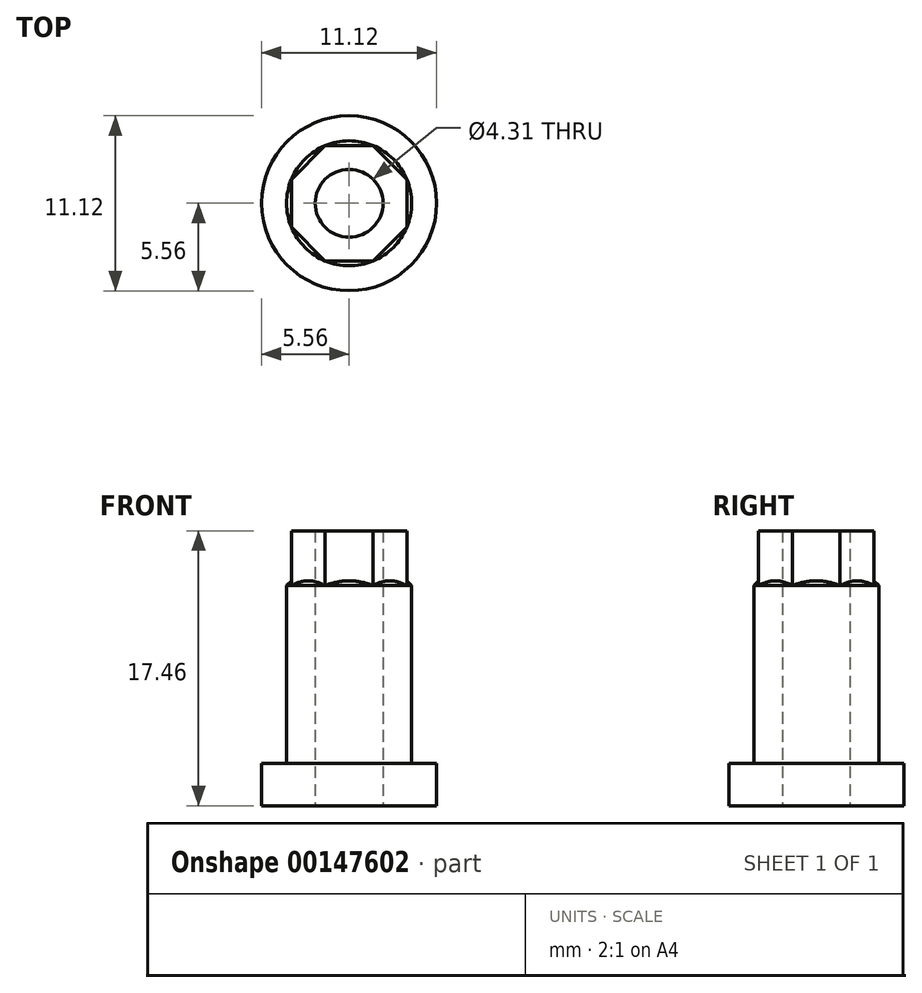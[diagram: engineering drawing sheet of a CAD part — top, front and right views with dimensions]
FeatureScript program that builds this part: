
annotation { "Feature Type Name" : "Feature", "Feature Type Description" : "" }
export const myFeature = defineFeature(function(context is Context, id is Id, definition is map)
    precondition{}
    {
        {
            var Q0;
            Q0=qCreatedBy(makeId("Top.planeOp"),FACE);
            var sketch = newSketch(context, id + "F0", { "sketchPlane" : qUnion([Q0])});
            skCircle(sketch, "E0", {"center": v(0, 0) * mm, "radius": 2.15 * mm});
            skCircle(sketch, "E1", {"center": v(0, 0) * mm, "radius": 5.56 * mm});
            skSolve(sketch);
        }
        {
            var Q0;
            Q0=qSketchRegion(id+"F0",true);
            extrude(context, id + "F1", {"entities" : qUnion([Q0]), "depth" : 2.7 * mm});
        }
        {
            var Q0;
            Q0=makeQuery(id+"F1.opExtrude","CAP_FACE",FACE,{"disambiguationData":[OSD([sQuery(id+"F0.wireOp",EDGE,"E0"),sQuery(id+"F0.wireOp",EDGE,"E1")])],"isStart":false});
            var sketch = newSketch(context, id + "F2", { "sketchPlane" : qUnion([Q0])});
            skCircle(sketch, "E2", {"center": v(0, 0) * mm, "radius": 2.15 * mm});
            skCircle(sketch, "E3", {"center": v(0, 0) * mm, "radius": 3.97 * mm});
            skSolve(sketch);
        }
        {
            var Q0;
            Q0=qSketchRegion(id+"F2",true);
            extrude(context, id + "F3", {"entities" : qUnion([Q0]), "operationType" : NewBodyOperationType.ADD, "depth" : 11.6 * mm});
        }
        {
            var Q0;
            Q0=makeQuery(id+"F3.opExtrude","CAP_FACE",FACE,{"disambiguationData":[OSD([sQuery(id+"F2.wireOp",EDGE,"E2"),sQuery(id+"F2.wireOp",EDGE,"E3")])],"isStart":false});
            var sketch = newSketch(context, id + "F4", { "sketchPlane" : qUnion([Q0])});
            skCircle(sketch, "E4", {"center": v(0, 0) * mm, "radius": 2.15 * mm});
            skCircle(sketch, "E5.cCircle", {"center": v(0, 0) * mm, "radius": 3.67 * mm, "construction": true});
            skLineSegment(sketch, "E5.0", {"start": v(-3.67, -1.52) * mm, "end": v(-3.67, 1.52) * mm});
            skLineSegment(sketch, "E5.1", {"start": v(-3.67, 1.52) * mm, "end": v(-1.52, 3.67) * mm});
            skLineSegment(sketch, "E5.2", {"start": v(-1.52, 3.67) * mm, "end": v(1.52, 3.67) * mm});
            skLineSegment(sketch, "E5.3", {"start": v(1.52, 3.67) * mm, "end": v(3.67, 1.52) * mm});
            skLineSegment(sketch, "E5.4", {"start": v(3.67, 1.52) * mm, "end": v(3.67, -1.52) * mm});
            skLineSegment(sketch, "E5.5", {"start": v(3.67, -1.52) * mm, "end": v(1.52, -3.67) * mm});
            skLineSegment(sketch, "E5.6", {"start": v(1.52, -3.67) * mm, "end": v(-1.52, -3.67) * mm});
            skLineSegment(sketch, "E5.7", {"start": v(-1.52, -3.67) * mm, "end": v(-3.67, -1.52) * mm});
            skSolve(sketch);
        }
        {
            var Q0;
            Q0=qSketchRegion(id+"F4",true);
            extrude(context, id + "F5", {"entities" : qUnion([Q0]), "operationType" : NewBodyOperationType.ADD, "depth" : 3.17 * mm});
        }
        {
            var Q0;
            {var subQ0=sQuery(id+"F2.wireOp",EDGE,"E3");Q0=makeQuery(id+"F5.boolean.opBoolean","SPLIT",EDGE,{"disambiguationData":[TD([makeQuery(id+"F3.opExtrude","CAP_FACE",FACE,{"disambiguationData":[OSD([sQuery(id+"F2.wireOp",EDGE,"E2"),subQ0])],"isStart":false}),makeQuery(id+"F3.opExtrude","SWEPT_FACE",FACE,{"disambiguationData":[OSD([subQ0])]}),makeQuery(id+"F5.opExtrude","SWEPT_FACE",FACE,{"disambiguationData":[OSD([sQuery(id+"F4.wireOp",EDGE,"E5.0")])]}),makeQuery(id+"F5.opExtrude","SWEPT_FACE",FACE,{"disambiguationData":[OSD([sQuery(id+"F4.wireOp",EDGE,"E5.1")])]}),makeQuery(id+"F5.opExtrude","SWEPT_FACE",FACE,{"disambiguationData":[OSD([sQuery(id+"F4.wireOp",EDGE,"E5.7")])]})])],"derivedFrom":makeQuery(id+"F3.opExtrude","CAP_EDGE",EDGE,{"disambiguationData":[OSD([subQ0])],"isStart":false})});}
            var Q1;
            {var subQ0=sQuery(id+"F2.wireOp",EDGE,"E3");Q1=makeQuery(id+"F5.boolean.opBoolean","SPLIT",EDGE,{"disambiguationData":[TD([makeQuery(id+"F3.opExtrude","CAP_FACE",FACE,{"disambiguationData":[OSD([sQuery(id+"F2.wireOp",EDGE,"E2"),subQ0])],"isStart":false}),makeQuery(id+"F3.opExtrude","SWEPT_FACE",FACE,{"disambiguationData":[OSD([subQ0])]}),makeQuery(id+"F5.opExtrude","SWEPT_FACE",FACE,{"disambiguationData":[OSD([sQuery(id+"F4.wireOp",EDGE,"E5.0")])]}),makeQuery(id+"F5.opExtrude","SWEPT_FACE",FACE,{"disambiguationData":[OSD([sQuery(id+"F4.wireOp",EDGE,"E5.1")])]}),makeQuery(id+"F5.opExtrude","SWEPT_FACE",FACE,{"disambiguationData":[OSD([sQuery(id+"F4.wireOp",EDGE,"E5.2")])]})])],"derivedFrom":makeQuery(id+"F3.opExtrude","CAP_EDGE",EDGE,{"disambiguationData":[OSD([subQ0])],"isStart":false})});}
            var Q2;
            {var subQ0=sQuery(id+"F2.wireOp",EDGE,"E3");Q2=makeQuery(id+"F5.boolean.opBoolean","SPLIT",EDGE,{"disambiguationData":[TD([makeQuery(id+"F3.opExtrude","CAP_FACE",FACE,{"disambiguationData":[OSD([sQuery(id+"F2.wireOp",EDGE,"E2"),subQ0])],"isStart":false}),makeQuery(id+"F3.opExtrude","SWEPT_FACE",FACE,{"disambiguationData":[OSD([subQ0])]}),makeQuery(id+"F5.opExtrude","SWEPT_FACE",FACE,{"disambiguationData":[OSD([sQuery(id+"F4.wireOp",EDGE,"E5.1")])]}),makeQuery(id+"F5.opExtrude","SWEPT_FACE",FACE,{"disambiguationData":[OSD([sQuery(id+"F4.wireOp",EDGE,"E5.2")])]}),makeQuery(id+"F5.opExtrude","SWEPT_FACE",FACE,{"disambiguationData":[OSD([sQuery(id+"F4.wireOp",EDGE,"E5.3")])]})])],"derivedFrom":makeQuery(id+"F3.opExtrude","CAP_EDGE",EDGE,{"disambiguationData":[OSD([subQ0])],"isStart":false})});}
            var Q3;
            {var subQ0=sQuery(id+"F2.wireOp",EDGE,"E3");Q3=makeQuery(id+"F5.boolean.opBoolean","SPLIT",EDGE,{"disambiguationData":[TD([makeQuery(id+"F3.opExtrude","CAP_FACE",FACE,{"disambiguationData":[OSD([sQuery(id+"F2.wireOp",EDGE,"E2"),subQ0])],"isStart":false}),makeQuery(id+"F3.opExtrude","SWEPT_FACE",FACE,{"disambiguationData":[OSD([subQ0])]}),makeQuery(id+"F5.opExtrude","SWEPT_FACE",FACE,{"disambiguationData":[OSD([sQuery(id+"F4.wireOp",EDGE,"E5.2")])]}),makeQuery(id+"F5.opExtrude","SWEPT_FACE",FACE,{"disambiguationData":[OSD([sQuery(id+"F4.wireOp",EDGE,"E5.3")])]}),makeQuery(id+"F5.opExtrude","SWEPT_FACE",FACE,{"disambiguationData":[OSD([sQuery(id+"F4.wireOp",EDGE,"E5.4")])]})])],"derivedFrom":makeQuery(id+"F3.opExtrude","CAP_EDGE",EDGE,{"disambiguationData":[OSD([subQ0])],"isStart":false})});}
            var Q4;
            {var subQ0=sQuery(id+"F2.wireOp",EDGE,"E3");Q4=makeQuery(id+"F5.boolean.opBoolean","SPLIT",EDGE,{"disambiguationData":[TD([makeQuery(id+"F3.opExtrude","CAP_FACE",FACE,{"disambiguationData":[OSD([sQuery(id+"F2.wireOp",EDGE,"E2"),subQ0])],"isStart":false}),makeQuery(id+"F3.opExtrude","SWEPT_FACE",FACE,{"disambiguationData":[OSD([subQ0])]}),makeQuery(id+"F5.opExtrude","SWEPT_FACE",FACE,{"disambiguationData":[OSD([sQuery(id+"F4.wireOp",EDGE,"E5.3")])]}),makeQuery(id+"F5.opExtrude","SWEPT_FACE",FACE,{"disambiguationData":[OSD([sQuery(id+"F4.wireOp",EDGE,"E5.4")])]}),makeQuery(id+"F5.opExtrude","SWEPT_FACE",FACE,{"disambiguationData":[OSD([sQuery(id+"F4.wireOp",EDGE,"E5.5")])]})])],"derivedFrom":makeQuery(id+"F3.opExtrude","CAP_EDGE",EDGE,{"disambiguationData":[OSD([subQ0])],"isStart":false})});}
            var Q5;
            {var subQ0=sQuery(id+"F2.wireOp",EDGE,"E3");Q5=makeQuery(id+"F5.boolean.opBoolean","SPLIT",EDGE,{"disambiguationData":[TD([makeQuery(id+"F3.opExtrude","CAP_FACE",FACE,{"disambiguationData":[OSD([sQuery(id+"F2.wireOp",EDGE,"E2"),subQ0])],"isStart":false}),makeQuery(id+"F3.opExtrude","SWEPT_FACE",FACE,{"disambiguationData":[OSD([subQ0])]}),makeQuery(id+"F5.opExtrude","SWEPT_FACE",FACE,{"disambiguationData":[OSD([sQuery(id+"F4.wireOp",EDGE,"E5.4")])]}),makeQuery(id+"F5.opExtrude","SWEPT_FACE",FACE,{"disambiguationData":[OSD([sQuery(id+"F4.wireOp",EDGE,"E5.5")])]}),makeQuery(id+"F5.opExtrude","SWEPT_FACE",FACE,{"disambiguationData":[OSD([sQuery(id+"F4.wireOp",EDGE,"E5.6")])]})])],"derivedFrom":makeQuery(id+"F3.opExtrude","CAP_EDGE",EDGE,{"disambiguationData":[OSD([subQ0])],"isStart":false})});}
            var Q6;
            {var subQ0=sQuery(id+"F2.wireOp",EDGE,"E3");Q6=makeQuery(id+"F5.boolean.opBoolean","SPLIT",EDGE,{"disambiguationData":[TD([makeQuery(id+"F3.opExtrude","CAP_FACE",FACE,{"disambiguationData":[OSD([sQuery(id+"F2.wireOp",EDGE,"E2"),subQ0])],"isStart":false}),makeQuery(id+"F3.opExtrude","SWEPT_FACE",FACE,{"disambiguationData":[OSD([subQ0])]}),makeQuery(id+"F5.opExtrude","SWEPT_FACE",FACE,{"disambiguationData":[OSD([sQuery(id+"F4.wireOp",EDGE,"E5.5")])]}),makeQuery(id+"F5.opExtrude","SWEPT_FACE",FACE,{"disambiguationData":[OSD([sQuery(id+"F4.wireOp",EDGE,"E5.6")])]}),makeQuery(id+"F5.opExtrude","SWEPT_FACE",FACE,{"disambiguationData":[OSD([sQuery(id+"F4.wireOp",EDGE,"E5.7")])]})])],"derivedFrom":makeQuery(id+"F3.opExtrude","CAP_EDGE",EDGE,{"disambiguationData":[OSD([subQ0])],"isStart":false})});}
            var Q7;
            {var subQ0=sQuery(id+"F2.wireOp",EDGE,"E3");Q7=makeQuery(id+"F5.boolean.opBoolean","SPLIT",EDGE,{"disambiguationData":[TD([makeQuery(id+"F3.opExtrude","CAP_FACE",FACE,{"disambiguationData":[OSD([sQuery(id+"F2.wireOp",EDGE,"E2"),subQ0])],"isStart":false}),makeQuery(id+"F3.opExtrude","SWEPT_FACE",FACE,{"disambiguationData":[OSD([subQ0])]}),makeQuery(id+"F5.opExtrude","SWEPT_FACE",FACE,{"disambiguationData":[OSD([sQuery(id+"F4.wireOp",EDGE,"E5.0")])]}),makeQuery(id+"F5.opExtrude","SWEPT_FACE",FACE,{"disambiguationData":[OSD([sQuery(id+"F4.wireOp",EDGE,"E5.6")])]}),makeQuery(id+"F5.opExtrude","SWEPT_FACE",FACE,{"disambiguationData":[OSD([sQuery(id+"F4.wireOp",EDGE,"E5.7")])]})])],"derivedFrom":makeQuery(id+"F3.opExtrude","CAP_EDGE",EDGE,{"disambiguationData":[OSD([subQ0])],"isStart":false})});}
            chamfer(context, id + "F6", {"entities" : qUnion([Q0, Q1, Q2, Q3, Q4, Q5, Q6, Q7]), "width" : 0.3 * mm, "tangentPropagation" : true});
        }
    });
